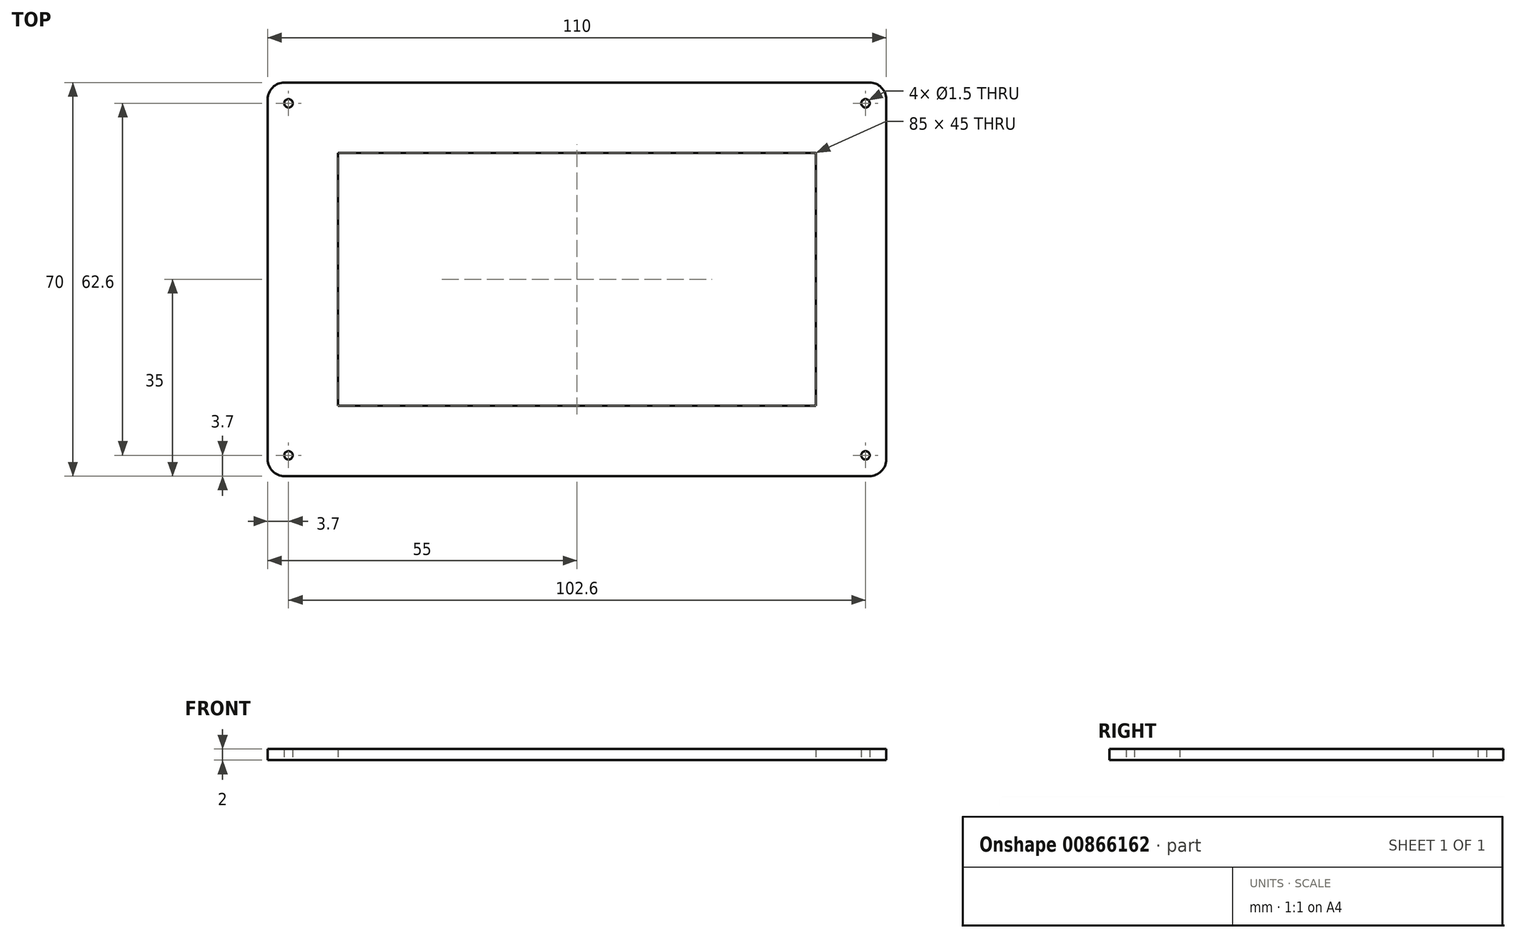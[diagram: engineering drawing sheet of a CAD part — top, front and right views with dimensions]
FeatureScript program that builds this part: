
annotation { "Feature Type Name" : "Feature", "Feature Type Description" : "" }
export const myFeature = defineFeature(function(context is Context, id is Id, definition is map)
    precondition{}
    {
        {
            var Q0;
            Q0=qCreatedBy(makeId("Top.planeOp"),FACE);
            var sketch = newSketch(context, id + "F0", { "sketchPlane" : qUnion([Q0])});
            skLineSegment(sketch, "E0.bottom", {"start": v(52, 35) * mm, "end": v(-52, 35) * mm});
            skLineSegment(sketch, "E0.top", {"start": v(52, -35) * mm, "end": v(-52, -35) * mm});
            skLineSegment(sketch, "E0.left", {"start": v(55, 32) * mm, "end": v(55, -32) * mm});
            skLineSegment(sketch, "E0.right", {"start": v(-55, 32) * mm, "end": v(-55, -32) * mm});
            skPoint(sketch, "E0.middle", {"position": v(0, 0) * mm});
            skLineSegment(sketch, "E1.bottom", {"start": v(42.5, 22.5) * mm, "end": v(-42.5, 22.5) * mm});
            skLineSegment(sketch, "E1.top", {"start": v(42.5, -22.5) * mm, "end": v(-42.5, -22.5) * mm});
            skLineSegment(sketch, "E1.left", {"start": v(42.5, 22.5) * mm, "end": v(42.5, -22.5) * mm});
            skLineSegment(sketch, "E1.right", {"start": v(-42.5, 22.5) * mm, "end": v(-42.5, -22.5) * mm});
            skPoint(sketch, "E2.visualSharp", {"position": v(-55, 35) * mm});
            skArc(sketch, "E2.filletArc", {"start": v(-52, 35) * mm, "mid": v(-54.12, 34.12) * mm, "end": v(-55, 32) * mm});
            skPoint(sketch, "E3.visualSharp", {"position": v(55, 35) * mm});
            skArc(sketch, "E3.filletArc", {"start": v(55, 32) * mm, "mid": v(54.12, 34.12) * mm, "end": v(52, 35) * mm});
            skPoint(sketch, "E4.visualSharp", {"position": v(-55, -35) * mm});
            skArc(sketch, "E4.filletArc", {"start": v(-55, -32) * mm, "mid": v(-54.12, -34.12) * mm, "end": v(-52, -35) * mm});
            skPoint(sketch, "E5.visualSharp", {"position": v(55, -35) * mm});
            skArc(sketch, "E5.filletArc", {"start": v(52, -35) * mm, "mid": v(54.12, -34.12) * mm, "end": v(55, -32) * mm});
            skCircle(sketch, "E6", {"center": v(-51.3, 31.3) * mm, "radius": 0.75 * mm});
            skCircle(sketch, "E7.MirrorC", {"center": v(-51.3, -31.3) * mm, "radius": 0.75 * mm});
            skCircle(sketch, "E8.MirrorC", {"center": v(51.3, 31.3) * mm, "radius": 0.75 * mm});
            skCircle(sketch, "E9.MirrorC", {"center": v(51.3, -31.3) * mm, "radius": 0.75 * mm});
            skSolve(sketch);
        }
        {
            var Q0;
            Q0=makeQuery(id+"F0.imprint","IMPRINT",FACE,{"disambiguationData":[TD([[makeQuery(id+"F0.imprint","IMPRINT",EDGE,{"derivedFrom":sQuery(id+"F0.wireOp",EDGE,"E0.bottom")}),1.0]])]});
            extrude(context, id + "F1", {"entities" : qUnion([Q0]), "depth" : 2 * mm, "offsetDistance" : 25 * mm});
        }
    });
